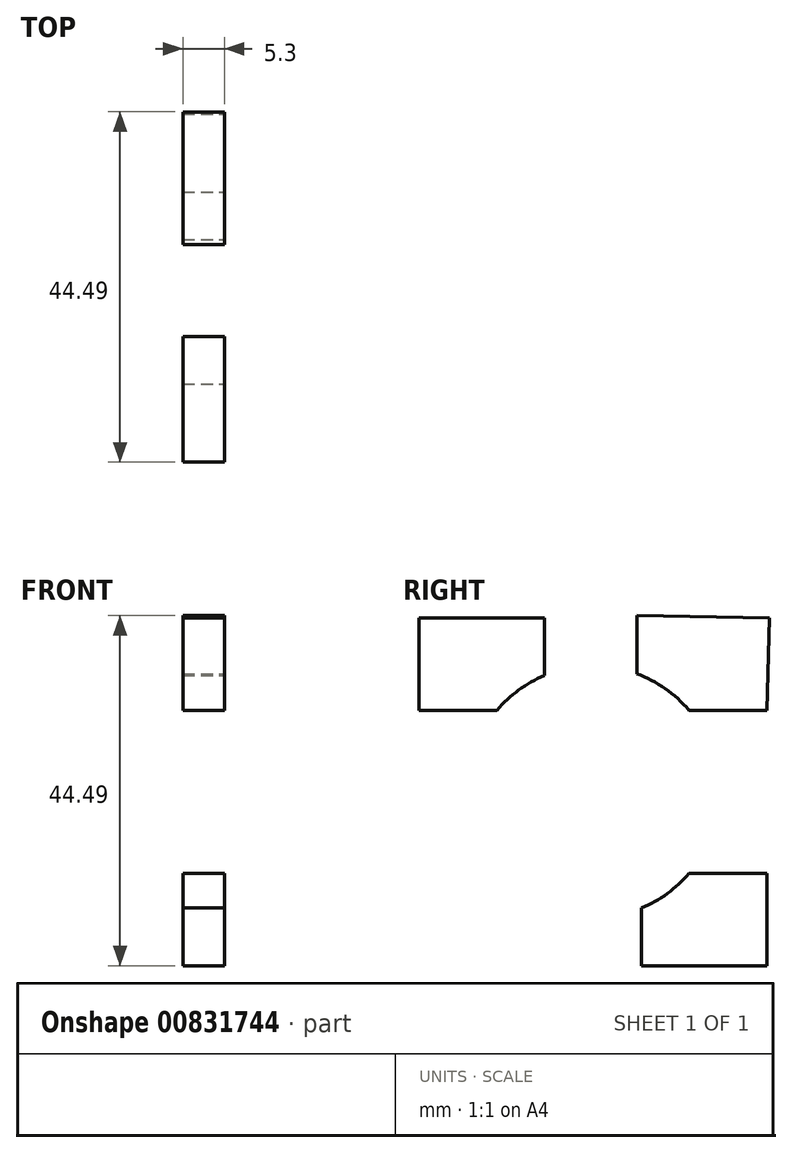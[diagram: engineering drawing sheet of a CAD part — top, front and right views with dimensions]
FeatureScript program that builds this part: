
annotation { "Feature Type Name" : "Feature", "Feature Type Description" : "" }
export const myFeature = defineFeature(function(context is Context, id is Id, definition is map)
    precondition{}
    {
        {
            var Q0;
            Q0=qCreatedBy(makeId("Right.planeOp"),FACE);
            var sketch = newSketch(context, id + "F0", { "sketchPlane" : qUnion([Q0])});
            skCircle(sketch, "E0", {"center": v(0.1, 0.46) * mm, "radius": 16 * mm});
            skLineSegment(sketch, "E1.top", {"start": v(-21.99, -21.93) * mm, "end": v(22.5, -21.93) * mm});
            skLineSegment(sketch, "E2.bottom", {"start": v(-21.99, 10.83) * mm, "end": v(-6.06, 10.83) * mm});
            skLineSegment(sketch, "E2.top", {"start": v(-21.99, 22.56) * mm, "end": v(-6.06, 22.56) * mm});
            skLineSegment(sketch, "E2.left", {"start": v(-21.99, 10.83) * mm, "end": v(-21.99, 22.56) * mm});
            skLineSegment(sketch, "E2.right", {"start": v(-6.06, 10.83) * mm, "end": v(-6.06, 22.56) * mm});
            skLineSegment(sketch, "E3.1.0", {"start": v(22.2, -9.9) * mm, "end": v(22.2, -21.63) * mm});
            skLineSegment(sketch, "E3.1.1", {"start": v(22.2, -9.9) * mm, "end": v(6.26, -9.9) * mm});
            skLineSegment(sketch, "E3.1.2", {"start": v(6.26, -9.9) * mm, "end": v(6.26, -21.63) * mm});
            skLineSegment(sketch, "E3.1.3", {"start": v(22.2, -21.63) * mm, "end": v(6.26, -21.63) * mm});
            skLineSegment(sketch, "E4.bottom", {"start": v(-21.99, -9.9) * mm, "end": v(-5.46, -9.9) * mm});
            skLineSegment(sketch, "E4.top", {"start": v(-21.99, -21.93) * mm, "end": v(-5.46, -21.93) * mm});
            skLineSegment(sketch, "E4.left", {"start": v(-21.99, -9.9) * mm, "end": v(-21.99, -21.93) * mm});
            skLineSegment(sketch, "E4.right", {"start": v(-5.46, -9.9) * mm, "end": v(-5.46, -21.93) * mm});
            skLineSegment(sketch, "E5.1.0", {"start": v(22.2, 10.83) * mm, "end": v(5.66, 10.83) * mm});
            skLineSegment(sketch, "E5.1.1", {"start": v(5.66, 10.83) * mm, "end": v(5.66, 22.86) * mm});
            skLineSegment(sketch, "E5.1.2", {"start": v(22.2, 22.86) * mm, "end": v(5.66, 22.86) * mm});
            skLineSegment(sketch, "E6", {"start": v(22.5, 22.56) * mm, "end": v(22.2, 10.83) * mm});
            skLineSegment(sketch, "E7", {"start": v(22.5, 22.56) * mm, "end": v(5.66, 22.86) * mm});
            skSolve(sketch);
        }
        {
            var Q0;
            {var subQ1=sQuery(id+"F0.wireOp",EDGE,"E2.top");Q0=makeQuery(id+"F0.imprint","IMPRINT",FACE,{"disambiguationData":[TD([[makeQuery(id+"F0.imprint","IMPRINT",EDGE,{"derivedFrom":subQ1}),-1.0]])]});}
            var Q1;
            {var subQ4=sQuery(id+"F0.wireOp",EDGE,"E6");Q1=makeQuery(id+"F0.imprint","IMPRINT",FACE,{"disambiguationData":[TD([[makeQuery(id+"F0.imprint","IMPRINT",EDGE,{"derivedFrom":subQ4}),-1.0]])]});}
            var Q2;
            {var subQ5=sQuery(id+"F0.wireOp",EDGE,"E3.1.0");Q2=makeQuery(id+"F0.imprint","IMPRINT",FACE,{"disambiguationData":[TD([[makeQuery(id+"F0.imprint","IMPRINT",EDGE,{"derivedFrom":subQ5}),-1.0]])]});}
            var Q3;
            {var subQ1=sQuery(id+"F0.wireOp",EDGE,"E4.top");Q3=makeQuery(id+"F0.imprint","IMPRINT",FACE,{"disambiguationData":[TD([[makeQuery(id+"F0.imprint","IMPRINT",EDGE,{"derivedFrom":subQ1}),1.0]])]});}
            extrude(context, id + "F1", {"entities" : qUnion([Q0, Q1, Q2, Q3]), "oppositeDirection" : true, "depth" : 5.3 * mm, "offsetDistance" : 25 * mm});
        }
    });
